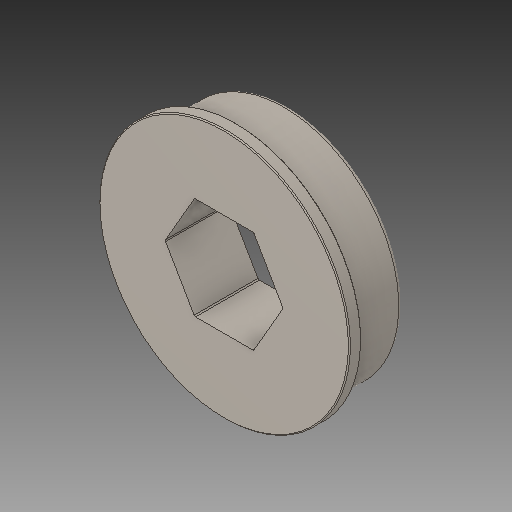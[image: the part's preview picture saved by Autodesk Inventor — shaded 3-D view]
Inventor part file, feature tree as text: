
AUTODESK INVENTOR PART (.ipt)
format: ipt  version: 2019 (Build 230136000, 136)  size: 145,920 bytes
history: native  units: in
note: dims shown in document units (in); Inventor stores cm internally (conversion verified against a paired STEP export)
features: fillet x1
ambient origin geometry x8: Origin, YZ Plane, XZ Plane, XY Plane, X Axis, Y Axis, Z Axis, Center Point
bodies: Solid1 (feature_tree)
feature tree (1):
  fillet  "Fillet2"  [1 undecoded]
note: 1 required parameter value undecoded (feature->parameter linkage not recoverable at this tier; creation-order binding heuristic only, values carry confidence <= 0.55)
